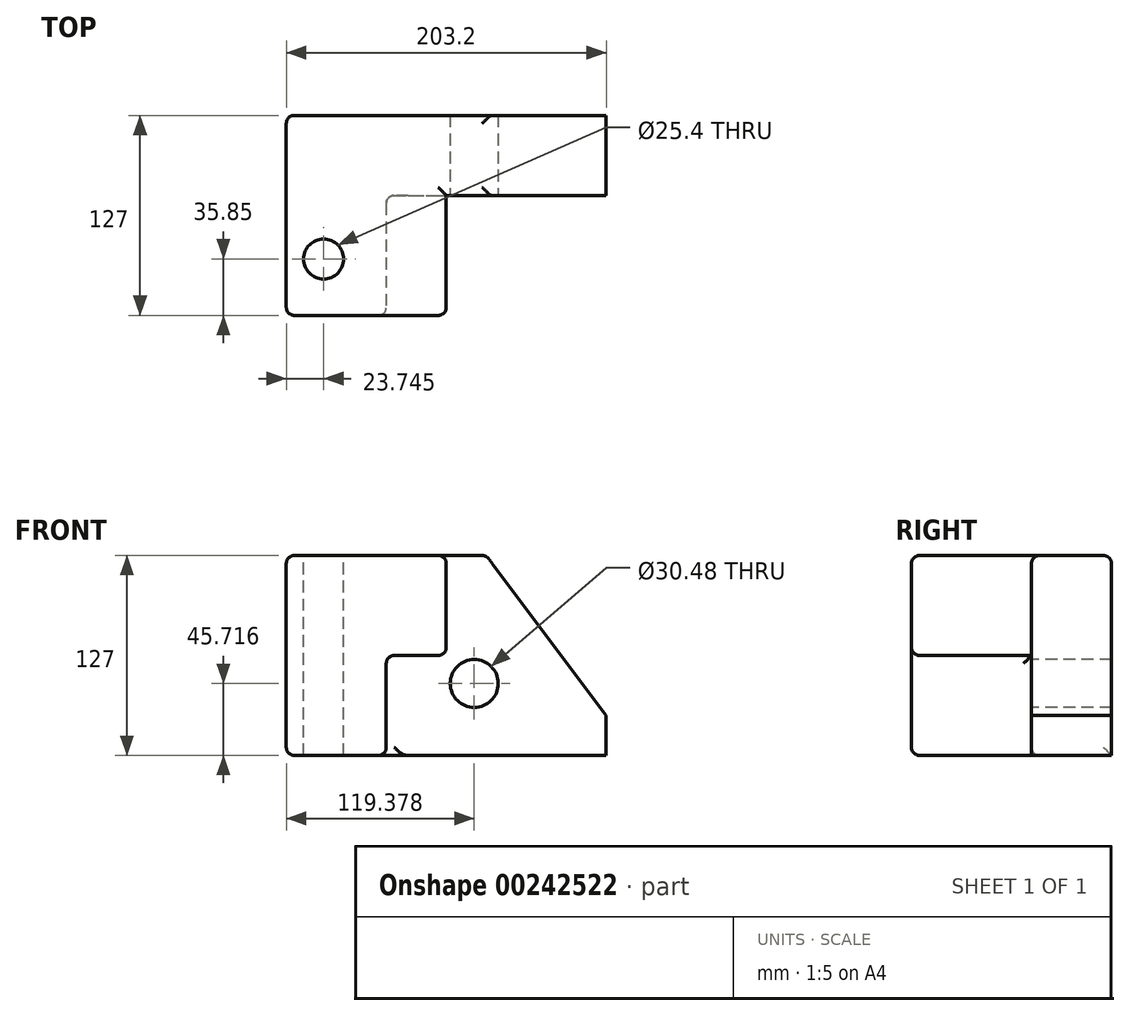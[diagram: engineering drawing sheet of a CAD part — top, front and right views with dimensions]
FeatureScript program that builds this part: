
annotation { "Feature Type Name" : "Feature", "Feature Type Description" : "" }
export const myFeature = defineFeature(function(context is Context, id is Id, definition is map)
    precondition{}
    {
        {
            var Q0;
            Q0=qCreatedBy(makeId("Front.planeOp"),FACE);
            var sketch = newSketch(context, id + "F0", { "sketchPlane" : qUnion([Q0])});
            skLineSegment(sketch, "E0.bottom", {"start": v(-86.28, 55.47) * mm, "end": v(116.92, 55.47) * mm});
            skLineSegment(sketch, "E0.top", {"start": v(-86.28, -71.53) * mm, "end": v(116.92, -71.53) * mm});
            skLineSegment(sketch, "E0.left", {"start": v(-86.28, 55.47) * mm, "end": v(-86.28, -71.53) * mm});
            skLineSegment(sketch, "E0.right", {"start": v(116.92, 55.47) * mm, "end": v(116.92, -71.53) * mm});
            skSolve(sketch);
        }
        {
            var Q0;
            Q0=makeQuery(id+"F0.imprint","IMPRINT",FACE,{"disambiguationData":[TD([[makeQuery(id+"F0.imprint","IMPRINT",EDGE,{"derivedFrom":sQuery(id+"F0.wireOp",EDGE,"E0.bottom")}),-1.0]])]});
            extrude(context, id + "F1", {"entities" : qUnion([Q0]), "depth" : 127 * mm});
        }
        {
            var Q0;
            Q0=makeQuery(id+"F1.opExtrude","CAP_FACE",FACE,{"disambiguationData":[OSD([sQuery(id+"F0.wireOp",EDGE,"E0.bottom"),sQuery(id+"F0.wireOp",EDGE,"E0.top"),sQuery(id+"F0.wireOp",EDGE,"E0.left"),sQuery(id+"F0.wireOp",EDGE,"E0.right")])],"isStart":false});
            var sketch = newSketch(context, id + "F2", { "sketchPlane" : qUnion([Q0])});
            skLineSegment(sketch, "E1", {"start": v(-86.28, -71.53) * mm, "end": v(-22.78, -71.53) * mm});
            skLineSegment(sketch, "E2", {"start": v(-22.78, -71.53) * mm, "end": v(-22.78, -8.03) * mm});
            skLineSegment(sketch, "E3", {"start": v(-22.78, -8.03) * mm, "end": v(15.32, -8.03) * mm});
            skLineSegment(sketch, "E4", {"start": v(15.32, -8.03) * mm, "end": v(15.32, 37.22) * mm});
            skLineSegment(sketch, "E5", {"start": v(15.32, 37.22) * mm, "end": v(15.32, 55.47) * mm});
            skSolve(sketch);
        }
        {
            var Q0;
            {var subQ3=sQuery(id+"F2.wireOp",EDGE,"E2");Q0=makeQuery(id+"F2.imprint","IMPRINT",FACE,{"disambiguationData":[TD([[makeQuery(id+"F2.imprint","IMPRINT",EDGE,{"derivedFrom":subQ3}),-1.0]])]});}
            extrude(context, id + "F3", {"entities" : qUnion([Q0]), "operationType" : NewBodyOperationType.REMOVE, "oppositeDirection" : true, "depth" : 76.2 * mm});
        }
        {
            var Q0;
            Q0=makeQuery(id+"F1.opExtrude","SWEPT_EDGE",EDGE,{"disambiguationData":[OSD([sQuery(id+"F0.wireOp",EDGE,"E0.bottom"),sQuery(id+"F0.wireOp",EDGE,"E0.right")])]});
            chamfer(context, id + "F4", {"entities" : qUnion([Q0]), "chamferType" : ChamferType.TWO_OFFSETS, "width1" : 76.2 * mm, "oppositeDirection" : false, "width2" : 101.6 * mm, "tangentPropagation" : true});
        }
        {
            var Q0;
            Q0=makeQuery(id+"F3.boolean.opBoolean","COPY",EDGE,{"derivedFrom":makeQuery(id+"F3.opExtrude","SWEPT_EDGE",EDGE,{"disambiguationData":[OSD([sQuery(id+"F0.wireOp",EDGE,"E0.bottom"),sQuery(id+"F2.wireOp",EDGE,"E5")])]})});
            var Q1;
            Q1=makeQuery(id+"F1.opExtrude","CAP_EDGE",EDGE,{"disambiguationData":[OSD([sQuery(id+"F0.wireOp",EDGE,"E0.bottom")])],"isStart":false});
            var Q2;
            Q2=makeQuery(id+"F3.boolean.opBoolean","COPY",EDGE,{"derivedFrom":makeQuery(id+"F3.opExtrude","CAP_EDGE",EDGE,{"disambiguationData":[OSD([sQuery(id+"F2.wireOp",EDGE,"E4"),sQuery(id+"F2.wireOp",EDGE,"E5")])],"isStart":true})});
            var Q3;
            Q3=makeQuery(id+"F3.boolean.opBoolean","COPY",EDGE,{"derivedFrom":makeQuery(id+"F3.opExtrude","SWEPT_EDGE",EDGE,{"disambiguationData":[OSD([sQuery(id+"F2.wireOp",EDGE,"E3"),sQuery(id+"F2.wireOp",EDGE,"E4")])]})});
            var Q4;
            Q4=makeQuery(id+"F3.boolean.opBoolean","COPY",FACE,{"derivedFrom":makeQuery(id+"F3.opExtrude","SWEPT_FACE",FACE,{"disambiguationData":[OSD([sQuery(id+"F2.wireOp",EDGE,"E2")])]})});
            var Q5;
            Q5=makeQuery(id+"F1.opExtrude","CAP_FACE",FACE,{"disambiguationData":[OSD([sQuery(id+"F0.wireOp",EDGE,"E0.bottom"),sQuery(id+"F0.wireOp",EDGE,"E0.top"),sQuery(id+"F0.wireOp",EDGE,"E0.left"),sQuery(id+"F0.wireOp",EDGE,"E0.right")])],"isStart":false});
            var Q6;
            Q6=makeQuery(id+"F1.opExtrude","SWEPT_FACE",FACE,{"disambiguationData":[OSD([sQuery(id+"F0.wireOp",EDGE,"E0.left")])]});
            var Q7;
            Q7=makeQuery(id+"F1.opExtrude","SWEPT_FACE",FACE,{"disambiguationData":[OSD([sQuery(id+"F0.wireOp",EDGE,"E0.bottom")])]});
            fillet(context, id + "F5", {"entities" : qUnion([Q0, Q1, Q2, Q3, Q4, Q5, Q6, Q7]), "radius" : 5.08 * mm, "tangentPropagation" : true, "allowEdgeOverflow" : false});
        }
        {
            var Q0;
            Q0=makeQuery(id+"F3.boolean.opBoolean","COPY",FACE,{"derivedFrom":makeQuery(id+"F3.opExtrude","CAP_FACE",FACE,{"disambiguationData":[OSD([sQuery(id+"F0.wireOp",EDGE,"E0.bottom"),sQuery(id+"F0.wireOp",EDGE,"E0.top"),sQuery(id+"F0.wireOp",EDGE,"E0.right"),sQuery(id+"F2.wireOp",EDGE,"E2"),sQuery(id+"F2.wireOp",EDGE,"E3"),sQuery(id+"F2.wireOp",EDGE,"E4"),sQuery(id+"F2.wireOp",EDGE,"E5")])],"isStart":false})});
            var sketch = newSketch(context, id + "F6", { "sketchPlane" : qUnion([Q0])});
            skCircle(sketch, "E6", {"center": v(33.1, -25.81) * mm, "radius": 15.24 * mm});
            skSolve(sketch);
        }
        {
            var Q0;
            Q0=makeQuery(id+"F6.imprint","IMPRINT",FACE,{"disambiguationData":[TD([[makeQuery(id+"F6.imprint","IMPRINT",EDGE,{"derivedFrom":sQuery(id+"F6.wireOp",EDGE,"E6")}),1.0]])]});
            var Q1;
            Q1=makeQuery(id+"F1.opExtrude","CAP_FACE",FACE,{"disambiguationData":[OSD([sQuery(id+"F0.wireOp",EDGE,"E0.bottom"),sQuery(id+"F0.wireOp",EDGE,"E0.top"),sQuery(id+"F0.wireOp",EDGE,"E0.left"),sQuery(id+"F0.wireOp",EDGE,"E0.right")])],"isStart":true});
            extrude(context, id + "F7", {"entities" : qUnion([Q0]), "operationType" : NewBodyOperationType.REMOVE, "endBound" : BoundingType.UP_TO_SURFACE, "oppositeDirection" : true, "endBoundEntityFace" : qUnion([Q1]), "depth" : 25.4 * mm});
        }
        {
            var Q0;
            Q0=makeQuery(id+"F1.opExtrude","SWEPT_FACE",FACE,{"disambiguationData":[OSD([sQuery(id+"F0.wireOp",EDGE,"E0.bottom")])]});
            var sketch = newSketch(context, id + "F8", { "sketchPlane" : qUnion([Q0])});
            skCircle(sketch, "E7", {"center": v(-62.53, -91.15) * mm, "radius": 12.7 * mm});
            skSolve(sketch);
        }
        {
            var Q0;
            Q0=makeQuery(id+"F8.imprint","IMPRINT",FACE,{"disambiguationData":[TD([[makeQuery(id+"F8.imprint","IMPRINT",EDGE,{"derivedFrom":sQuery(id+"F8.wireOp",EDGE,"E7")}),1.0]])]});
            var Q1;
            Q1=makeQuery(id+"F1.opExtrude","SWEPT_FACE",FACE,{"disambiguationData":[OSD([sQuery(id+"F0.wireOp",EDGE,"E0.top")])]});
            extrude(context, id + "F9", {"entities" : qUnion([Q0]), "operationType" : NewBodyOperationType.REMOVE, "endBound" : BoundingType.UP_TO_SURFACE, "oppositeDirection" : true, "endBoundEntityFace" : qUnion([Q1]), "depth" : 25.4 * mm});
        }
    });
